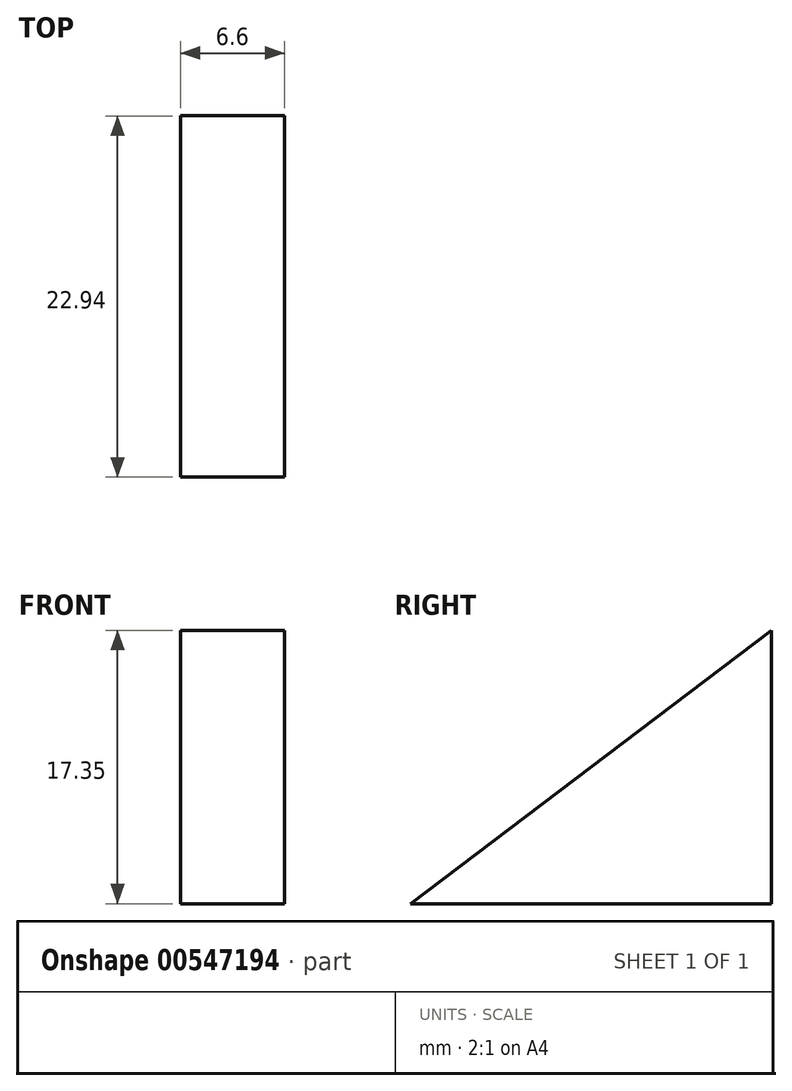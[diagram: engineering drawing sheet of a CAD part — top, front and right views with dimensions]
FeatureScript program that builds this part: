
annotation { "Feature Type Name" : "Feature", "Feature Type Description" : "" }
export const myFeature = defineFeature(function(context is Context, id is Id, definition is map)
    precondition{}
    {
        {
            var Q0;
            Q0=qCreatedBy(makeId("Right.planeOp"),FACE);
            var sketch = newSketch(context, id + "F0", { "sketchPlane" : qUnion([Q0])});
            skLineSegment(sketch, "E0", {"start": v(0, 0) * mm, "end": v(22.94, 0) * mm});
            skLineSegment(sketch, "E1", {"start": v(22.94, 0) * mm, "end": v(22.94, 17.35) * mm});
            skLineSegment(sketch, "E2", {"start": v(22.94, 17.35) * mm, "end": v(0, 0) * mm});
            skSolve(sketch);
        }
        {
            var Q0;
            Q0=makeQuery(id+"F0.imprint","IMPRINT",FACE,{"disambiguationData":[TD([[makeQuery(id+"F0.imprint","IMPRINT",EDGE,{"derivedFrom":sQuery(id+"F0.wireOp",EDGE,"E0")}),1.0]])]});
            extrude(context, id + "F1", {"entities" : qUnion([Q0]), "depth" : 6.6 * mm, "offsetDistance" : 25.4 * mm});
        }
    });
